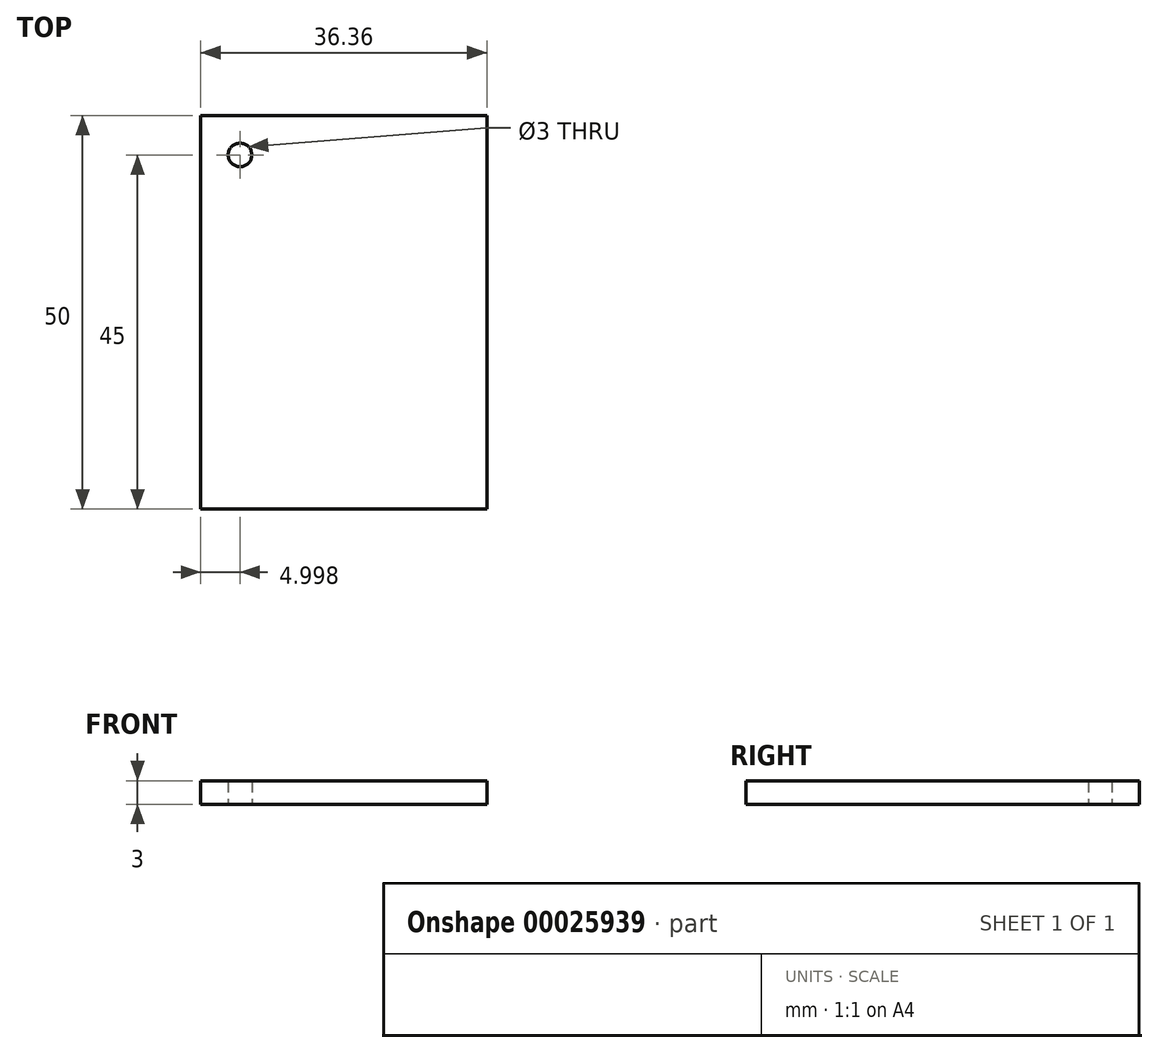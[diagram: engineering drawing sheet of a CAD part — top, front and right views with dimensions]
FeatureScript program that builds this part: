
annotation { "Feature Type Name" : "Feature", "Feature Type Description" : "" }
export const myFeature = defineFeature(function(context is Context, id is Id, definition is map)
    precondition{}
    {
        {
            var Q0;
            Q0=qCreatedBy(makeId("Top.planeOp"),FACE);
            var sketch = newSketch(context, id + "F0", { "sketchPlane" : qUnion([Q0])});
            skLineSegment(sketch, "E0.left", {"start": v(-19.4, 35.32) * mm, "end": v(-19.4, -14.68) * mm});
            skLineSegment(sketch, "E0.right", {"start": v(16.97, 35.32) * mm, "end": v(16.97, -14.68) * mm});
            skLineSegment(sketch, "E1", {"start": v(-19.4, 35.32) * mm, "end": v(16.97, 35.32) * mm});
            skLineSegment(sketch, "E2", {"start": v(16.97, -14.68) * mm, "end": v(-19.4, -14.68) * mm});
            skLineSegment(sketch, "E3.0", {"start": v(-19.4, 30.32) * mm, "end": v(16.97, 30.32) * mm, "construction": true});
            skLineSegment(sketch, "E4.0", {"start": v(-14.4, 35.32) * mm, "end": v(-14.4, -14.68) * mm, "construction": true});
            skCircle(sketch, "E5", {"center": v(-14.4, 30.32) * mm, "radius": 1.5 * mm});
            skSolve(sketch);
        }
        {
            var Q0;
            Q0=makeQuery(id+"F0.imprint","IMPRINT",FACE,{"disambiguationData":[TD([[makeQuery(id+"F0.imprint","IMPRINT",EDGE,{"derivedFrom":sQuery(id+"F0.wireOp",EDGE,"E0.left")}),1.0]])]});
            extrude(context, id + "F1", {"entities" : qUnion([Q0]), "depth" : 3 * mm});
        }
    });
